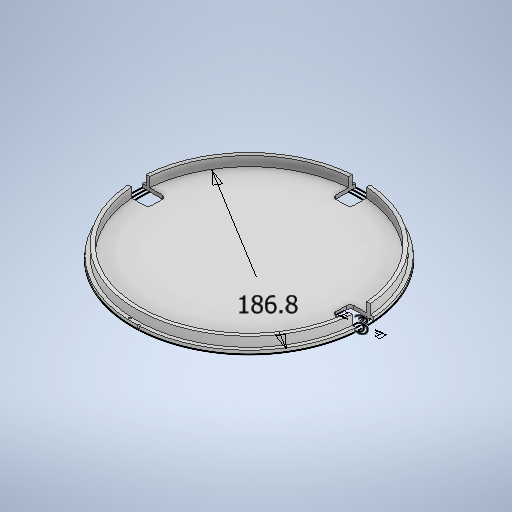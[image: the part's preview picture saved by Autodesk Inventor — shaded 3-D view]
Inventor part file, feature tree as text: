
AUTODESK INVENTOR PART (.ipt)
format: ipt  version: 2025.3 (Build 293356000, 356)  size: 644,608 bytes
history: native  units: in
note: dims shown in document units (in); Inventor stores cm internally (conversion verified against a paired STEP export)
features: extrude x5, sketch x3, pattern_circular x1, fillet x1
ambient origin geometry x8: Origin, YZ Plane, XZ Plane, XY Plane, X Axis, Y Axis, Z Axis, Center Point
bodies: Solid1 (feature_tree)
feature tree (10):
  sketch  "Sketch1"  dims[d0=7.3543in d1=0.1181in]
  extrude  "Extrusion1"  Depth=0.1181in
  extrude  "Extrusion2"  Depth=0.4331in TaperAngle=0.0deg
  extrude  "Extrusion3"  Depth=0.1181in
  extrude  "Extrusion4"  Depth=0.1181in
  extrude  "Extrusion5"  Depth=0.1181in
  pattern_circular  "Circular Pattern1"  [2 undecoded]
  fillet  "Fillet1"  Radius=0.1181in
  sketch  "Sketch2"  dims[d2=0.1181in d3=0.4331in d4=0.0in]
  sketch  "Sketch3"  dims[d5=0.1181in d6=0.0in d7=0.0787in d8=0.1772in d9=0.1772in d10=0.1181in d11=0.0in d12=0.1181in d13=0.0in d14=0.5906in d15=0.7874in d16=0.1181in d17=0.0in d18=1.1811in d19=180.0deg d21=0.1181in]
note: 2 required parameter values undecoded (feature->parameter linkage not recoverable at this tier; creation-order binding heuristic only, values carry confidence <= 0.55)
